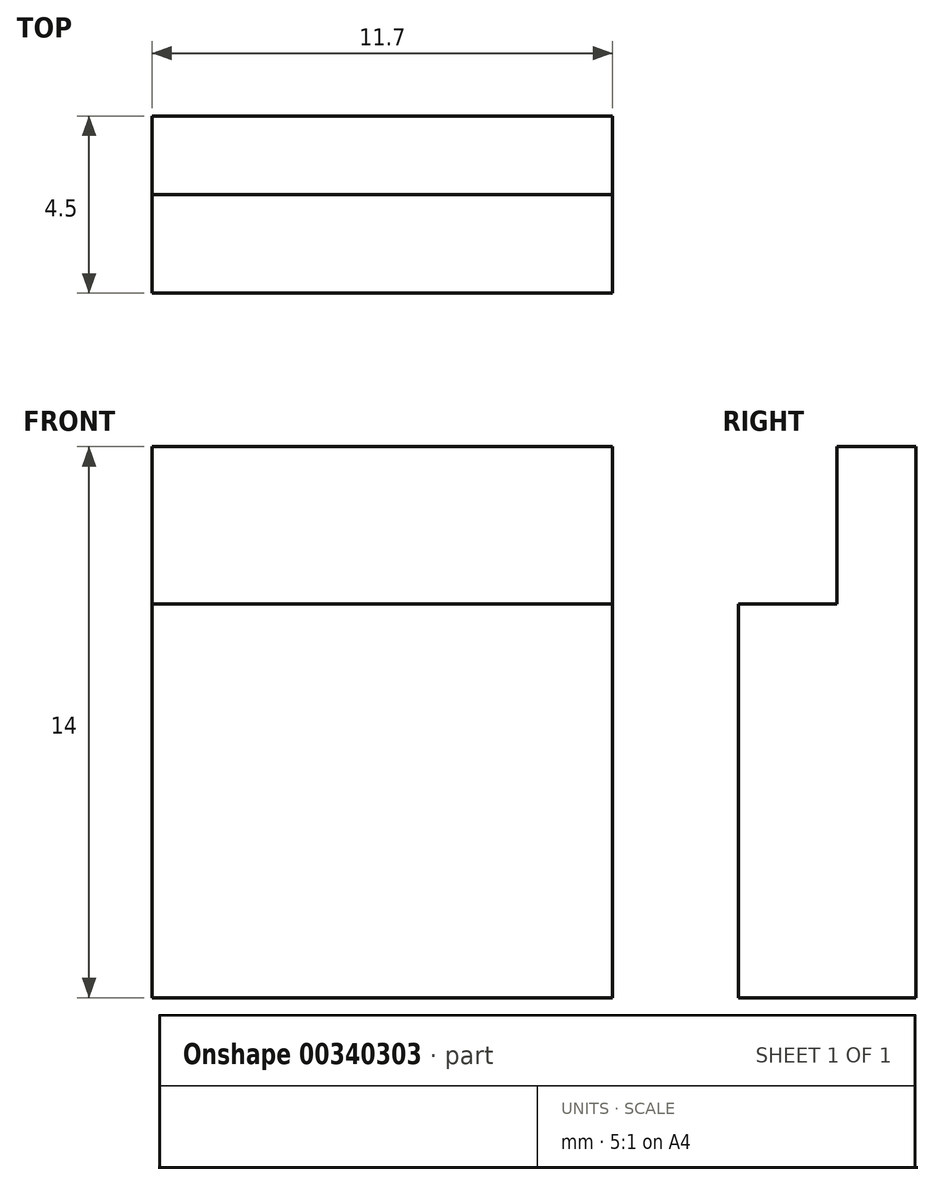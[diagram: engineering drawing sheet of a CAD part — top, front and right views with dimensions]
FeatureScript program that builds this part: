
annotation { "Feature Type Name" : "Feature", "Feature Type Description" : "" }
export const myFeature = defineFeature(function(context is Context, id is Id, definition is map)
    precondition{}
    {
        {
            var Q0;
            Q0=qCreatedBy(makeId("Front.planeOp"),FACE);
            var sketch = newSketch(context, id + "F0", { "sketchPlane" : qUnion([Q0])});
            skLineSegment(sketch, "E0.bottom", {"start": v(5.85, 7) * mm, "end": v(-5.85, 7) * mm});
            skLineSegment(sketch, "E0.top", {"start": v(5.85, -7) * mm, "end": v(-5.85, -7) * mm});
            skLineSegment(sketch, "E0.left", {"start": v(5.85, 7) * mm, "end": v(5.85, -7) * mm});
            skLineSegment(sketch, "E0.right", {"start": v(-5.85, 7) * mm, "end": v(-5.85, -7) * mm});
            skPoint(sketch, "E0.middle", {"position": v(0, 0) * mm});
            skSolve(sketch);
        }
        {
            var Q0;
            Q0 = qSketchRegion(id + "F0", true);
            extrude(context, id + "F1", {"entities" : qUnion([Q0]), "depth" : 2 * mm});
        }
        {
            var Q0;
            Q0=makeQuery(id+"F1.opExtrude","SWEPT_FACE",FACE,{"disambiguationData":[OSD([sQuery(id+"F0.wireOp",EDGE,"E0.left")])]});
            var sketch = newSketch(context, id + "F2", { "sketchPlane" : qUnion([Q0])});
            skLineSegment(sketch, "E1.bottom", {"start": v(-2, -7) * mm, "end": v(-4.5, -7) * mm});
            skLineSegment(sketch, "E1.top", {"start": v(-2, 3) * mm, "end": v(-4.5, 3) * mm});
            skLineSegment(sketch, "E1.left", {"start": v(-2, -7) * mm, "end": v(-2, 3) * mm});
            skLineSegment(sketch, "E1.right", {"start": v(-4.5, -7) * mm, "end": v(-4.5, 3) * mm});
            skSolve(sketch);
        }
        {
            var Q0;
            Q0 = qSketchRegion(id + "F2", true);
            extrude(context, id + "F3", {"entities" : qUnion([Q0]), "operationType" : NewBodyOperationType.ADD, "oppositeDirection" : true, "depth" : 11.7 * mm});
        }
    });
